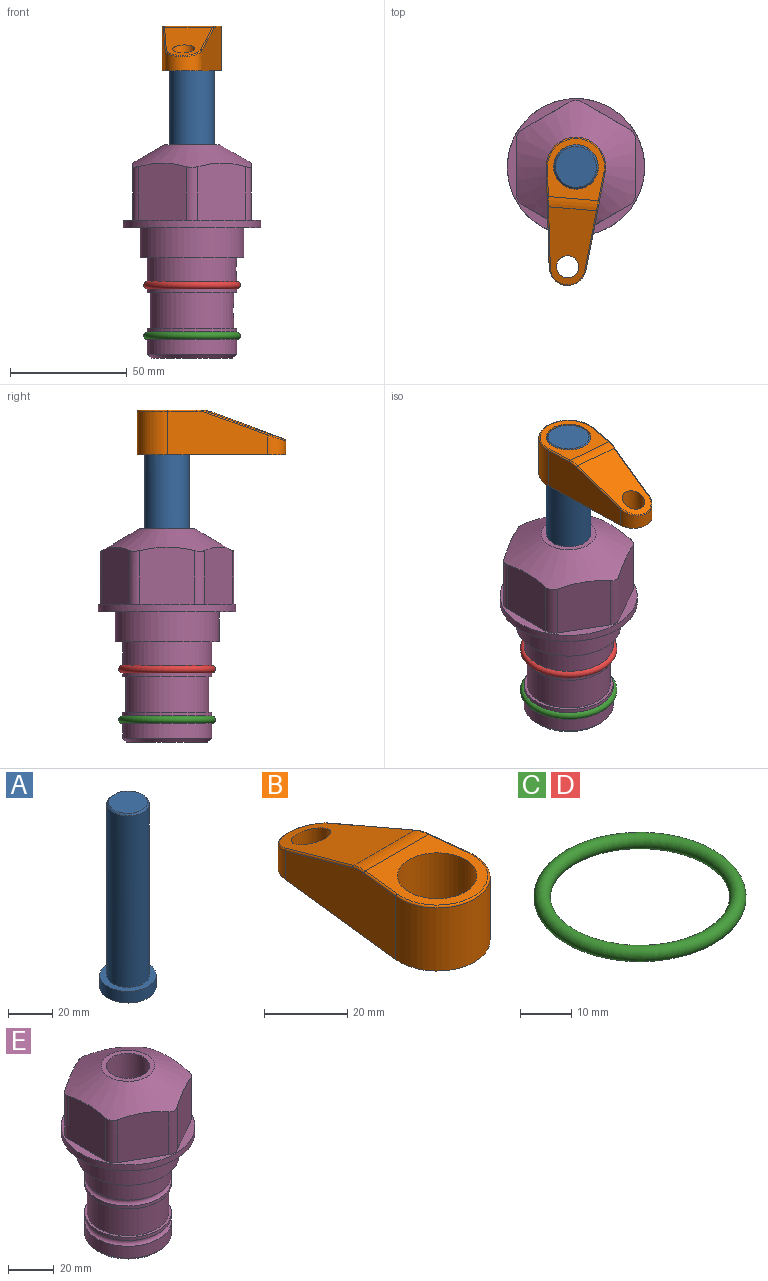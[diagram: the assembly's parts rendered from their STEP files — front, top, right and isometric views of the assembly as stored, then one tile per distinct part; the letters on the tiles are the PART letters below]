
ASSEMBLY  parts=5 mates=3
PART A: 6 faces, bbox 25.4x25.4x101.6 mm
  f0: plane 17.46x17.46mm, normal (0,0,1), area 239.5mm2, adj f5
  f1: plane 25.4x25.4mm, normal (0,0,-1), area 506.7mm2, adj f2
  f2: cylinder r=12.7mm len=25.4mm, axis (0,0,1), area 506.7mm2, adj f1,f3
  f3: plane 25.4x25.4mm, normal (0,0,1), area 221.7mm2, adj f2,f4
  f4: cylinder r=9.53mm len=94.46mm, axis (0,0,1), area 5653mm2, adj f3,f5
  f5: cone r=8.73mm half-angle=45deg, axis (0,0,-1), area 64.4mm2, adj f0,f4
PART B: 44 faces, bbox 27.5x64.5x19.1 mm
  f0: plane 2.3x0.95mm, normal (0,0,-1), area 1mm2, adj f25,f30,f34
  f1: plane 63.5x25.4mm, normal (0,0,-1), area 561.7mm2, adj f2,f3,f4,f5,f6,f7,f19,f20
  f2: cylinder r=12.7mm len=25.4mm, axis (0,0,-1), area 792.2mm2, adj f1,f3,f5,f13
  f3: plane 42.33x18.54mm, normal (0.99,0.11,0), area 647mm2, adj f1,f2,f4,f11,f12,f14
  f4: cylinder r=7.94mm len=15.78mm, axis (0,0,-1), area 158.6mm2, adj f1,f3,f5,f16
  f5: plane 42.33x18.54mm, normal (-0.99,0.11,0), area 647mm2, adj f1,f2,f4,f15,f17,f18
  f6: cylinder r=9.53mm len=19.05mm, axis (0,0,-1), area 1140.1mm2, adj f1,f8
  f7: cylinder r=4.76mm len=10.98mm, axis (0,0,-1), area 276.1mm2, adj f1,f9
  f8: plane 25.83x24.38mm, normal (0,0,1), area 262.2mm2, adj f6,f10,f11,f13,f15
  f9: plane 32.49x20.55mm, normal (0,0.34,0.94), area 489.9mm2, adj f7,f10,f14,f16,f18
  f10: cylinder r=12.7mm len=21.49mm, axis (-1,0,0), area 93.2mm2, adj f8,f9,f12,f17
  f11: cylinder r=0.51mm len=12.34mm, axis (0.11,-0.99,0), area 9.9mm2, adj f3,f8,f12,f13
  f12: bspline ~7.62x1.64mm, area 3.5mm2, adj f3,f10,f11,f14
  f13: torus R=12.19mm, axis (0,0,1), area 33.6mm2, adj f2,f8,f11,f15
  f14: cylinder r=0.51mm len=26.01mm, axis (0.1,-0.93,0.34), area 21.6mm2, adj f3,f9,f12,f16
  f15: cylinder r=0.51mm len=12.34mm, axis (0.11,0.99,0), area 9.9mm2, adj f5,f8,f13,f17
  f16: bspline ~15.78x7.05mm, area 15.7mm2, adj f4,f9,f14,f18
  f17: bspline ~7.62x1.64mm, area 3.5mm2, adj f5,f10,f15,f18
  f18: cylinder r=0.51mm len=26.01mm, axis (0.1,0.93,-0.34), area 21.6mm2, adj f5,f9,f16,f17
  f19: plane 21.6x14.29mm, normal (-0.99,-0.11,0), area 242.6mm2, adj f1,f26,f28,f34,f36,f38
  f20: plane 21.6x14.29mm, normal (0.99,-0.11,0), area 242.6mm2, adj f1,f27,f29,f37,f39,f41
  f21: cylinder r=12.7mm len=14.29mm, axis (0,0,-1), area 173.2mm2, adj f1,f26,f27,f30,f31,f33
  f22: cylinder r=7.94mm len=7.63mm, axis (0,0,-1), area 53.8mm2, adj f1,f28,f29,f42
  f23: plane 2.3x0.95mm, normal (0,0,-1), area 1mm2, adj f25,f33,f37
  f24: plane 17.94x12.32mm, normal (0,-0.34,-0.94), area 191.2mm2, adj f25,f38,f41,f42
  f25: cylinder r=9.53mm len=12.93mm, axis (-1,0,0), area 37.5mm2, adj f0,f23,f24,f31,f36,f39
  f26: cylinder r=1.59mm len=14.29mm, axis (0,0,-1), area 49mm2, adj f1,f19,f21,f32
  f27: cylinder r=1.59mm len=14.29mm, axis (0,0,-1), area 49mm2, adj f1,f20,f21,f35
  f28: cylinder r=1.59mm len=7.28mm, axis (0,0,-1), area 22.1mm2, adj f1,f19,f22,f40
  f29: cylinder r=1.59mm len=7.28mm, axis (0,0,-1), area 22.1mm2, adj f1,f20,f22,f43
  f30: torus R=14.29mm, axis (0,0,1), area 5.8mm2, adj f0,f21,f31,f32
  f31: bspline ~11.06x2.73mm, area 20.8mm2, adj f21,f25,f30,f33
  f32: sphere r=1.59mm, area 5.4mm2, adj f26,f30,f34
  f33: torus R=14.29mm, axis (0,0,1), area 5.8mm2, adj f21,f23,f31,f35
  f34: cylinder r=1.59mm len=1.68mm, axis (-0.11,0.99,0), area 2.4mm2, adj f0,f19,f32,f36
  f35: sphere r=1.59mm, area 5.4mm2, adj f27,f33,f37
  f36: bspline ~5.82x2.33mm, area 7.7mm2, adj f19,f25,f34,f38
  f37: cylinder r=1.59mm len=1.68mm, axis (0.11,0.99,0), area 2.4mm2, adj f20,f23,f35,f39
  f38: cylinder r=1.59mm len=18.33mm, axis (0.1,-0.93,0.34), area 46.7mm2, adj f19,f24,f36,f40
  f39: bspline ~5.82x2.33mm, area 7.7mm2, adj f20,f25,f37,f41
  f40: sphere r=1.59mm, area 3.6mm2, adj f28,f38,f42
  f41: cylinder r=1.59mm len=18.33mm, axis (0.1,0.93,-0.34), area 46.7mm2, adj f20,f24,f39,f43
  f42: bspline ~8.31x1.84mm, area 15.3mm2, adj f22,f24,f40,f43
  f43: sphere r=1.59mm, area 3.6mm2, adj f29,f41,f42
PART C: 1 faces, bbox 44.7x44.7x3.2 mm
  f0: torus R=19.05mm, axis (0,0,1), area 1193.9mm2
PART D: same geometry as C
PART E: 36 faces, bbox 58.7x58.7x91.2 mm
  f0: cylinder r=17.78mm len=35.56mm, axis (0,0,1), area 1670.8mm2, adj f23,f24,f31
  f1: cylinder r=19.05mm len=38.1mm, axis (0,0,1), area 1191.9mm2, adj f26,f27,f30
  f2: plane 58.66x58.66mm, normal (0,0,-1), area 1150.6mm2, adj f3,f28
  f3: cylinder r=29.33mm len=58.66mm, axis (0,0,-1), area 585.1mm2, adj f2,f4
  f4: plane 58.66x58.66mm, normal (0,0,1), area 475.9mm2, adj f3,f5,f6,f7,f8,f9,f10,f11
  f5: plane 24.5x20.32mm, normal (-0.5,0.87,0), area 562.8mm2, adj f4,f15,f16,f17
  f6: plane 24.5x20.32mm, normal (0.5,0.87,0), area 562.8mm2, adj f4,f14,f15,f17
  f7: plane 24.5x23.48mm, normal (1,0,0), area 562.8mm2, adj f4,f13,f14,f17
  f8: plane 24.5x20.32mm, normal (0.5,-0.87,0), area 562.8mm2, adj f4,f12,f13,f17
  f9: plane 24.5x20.32mm, normal (-0.5,-0.87,0), area 562.8mm2, adj f4,f11,f12,f17
  f10: plane 24.5x23.48mm, normal (-1,0,0), area 562.8mm2, adj f4,f11,f16,f17
  f11: cylinder r=5.08mm len=23.01mm, axis (0,0,-1), area 121.2mm2, adj f4,f9,f10,f17
  f12: cylinder r=5.08mm len=23.01mm, axis (0,0,-1), area 121.2mm2, adj f4,f8,f9,f17
  f13: cylinder r=5.08mm len=23.01mm, axis (0,0,-1), area 121.2mm2, adj f4,f7,f8,f17
  f14: cylinder r=5.08mm len=23.01mm, axis (0,0,-1), area 121.2mm2, adj f4,f6,f7,f17
  f15: cylinder r=5.08mm len=23.01mm, axis (0,0,-1), area 121.2mm2, adj f4,f5,f6,f17
  f16: cylinder r=5.08mm len=23.01mm, axis (0,0,-1), area 121.2mm2, adj f4,f5,f10,f17
  f17: cone r=11.73mm half-angle=60deg, axis (0,0,-1), area 2071.8mm2, adj f5,f6,f7,f8,f9,f10,f11,f12
  f18: plane 23.46x23.46mm, normal (0,0,1), area 147.4mm2, adj f17,f35
  f19: plane 34.93x34.93mm, normal (0,0,-1), area 958mm2, adj f29
  f20: cylinder r=19.05mm len=38.1mm, axis (0,0,1), area 760.1mm2, adj f21,f29
  f21: torus R=19.05mm, axis (0,0,1), area 565.3mm2, adj f20,f22
  f22: cylinder r=19.05mm len=38.1mm, axis (0,0,1), area 190mm2, adj f21,f23
  f23: plane 38.1x38.1mm, normal (0,0,1), area 146.9mm2, adj f0,f22
  f24: plane 38.1x38.1mm, normal (0,0,-1), area 146.9mm2, adj f0,f25
  f25: cylinder r=19.05mm len=38.1mm, axis (0,0,1), area 190mm2, adj f24,f26
  f26: torus R=19.05mm, axis (0,0,1), area 565.3mm2, adj f1,f25
  f27: plane 44.45x44.45mm, normal (0,0,-1), area 411.7mm2, adj f1,f28
  f28: cylinder r=22.23mm len=44.45mm, axis (0,0,1), area 1773.5mm2, adj f2,f27
  f29: cone r=19.05mm half-angle=45deg, axis (0,0,1), area 257.5mm2, adj f19,f20
  f30: cylinder r=3.17mm len=6.75mm, axis (-1,0,0), area 128mm2, adj f1,f33
  f31: cylinder r=3.17mm len=6.35mm, axis (-1,0,0), area 102.5mm2, adj f0,f33
  f32: plane 25.4x25.4mm, normal (0,0,1), area 506.7mm2, adj f33
  f33: cylinder r=12.7mm len=66.42mm, axis (0,0,-1), area 5236.2mm2, adj f30,f31,f32,f34
  f34: cone r=9.53mm half-angle=30deg, axis (0,0,-1), area 443.4mm2, adj f33,f35
  f35: cylinder r=9.53mm len=19.05mm, axis (0,0,-1), area 849mm2, adj f18,f34
PLACE A rot(axis=(0,0,-1),94.7deg) t=(0,0,12.61)mm
PLACE B rot(axis=(0,0,1),175.3deg) t=(0,0,67.22)mm
PLACE C t=(0,0,-21.59)mm
PLACE D at identity
PLACE E at identity fixed
MATE fastened C.f0 <-> E.f0  axis (0,0,1) through (0,0,-46.1)mm
MATE cylindrical A.f2 <-> E.f0  axis (0,0,1) through (0,0,38.25)mm
MATE fastened B.f2 <-> A.f2  axis (0,0,1) through (0,0,86.27)mm
